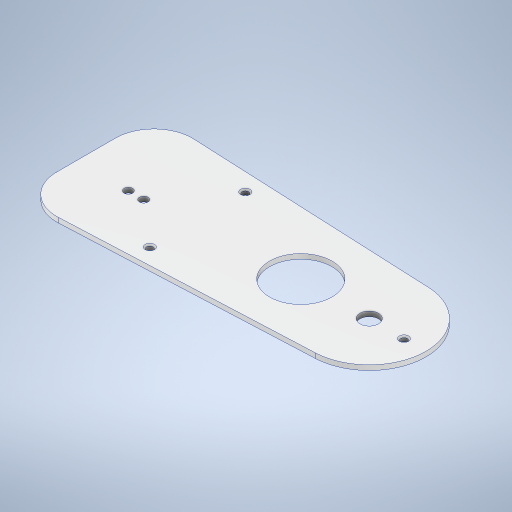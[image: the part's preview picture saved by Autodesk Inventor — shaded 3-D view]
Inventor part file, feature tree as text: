
AUTODESK INVENTOR PART (.ipt)
format: ipt  version: 2023 (Build 270158000, 158)  size: 285,184 bytes
history: native  units: in
note: dims shown in document units (in); Inventor stores cm internally (conversion verified against a paired STEP export)
features: extrude x3, sketch x3, hole x1
ambient origin geometry x8: Origin, YZ Plane, XZ Plane, XY Plane, X Axis, Y Axis, Z Axis, Center Point
bodies: Solid1 (feature_tree)
feature tree (7):
  extrude  "Main"  Depth=6.2598in
  extrude  "Axis Holes"  Depth=1.45in
  extrude  "Extrusion6"  Depth=0.2362in
  hole  "Hole1"  [1 undecoded]
  sketch  "Sketch1"  dims[d0=1.9685in d1=6.2598in]
  sketch  "Sketch5"  dims[d2=1.5in d3=1.45in]
  sketch  "Sketch9"  dims[d4=0.125in d5=0.0in d6=1.5945in d7=0.0in d8=0.0in d40=0.4724in d41=1.751in d43=2.0in d44=0.2756in d45=0.3937in d46=0.2165in d47=0.0in d48=0.0in d66=0.1628in d67=0.3937in d68=0.2362in d69=0.0787in d70=90.0deg d71=0.315in d72=0.8108in d73=2.6401in d74=2.6401in d75=1.2205in d76=1.2205in]
note: 1 required parameter value undecoded (feature->parameter linkage not recoverable at this tier; creation-order binding heuristic only, values carry confidence <= 0.55)
